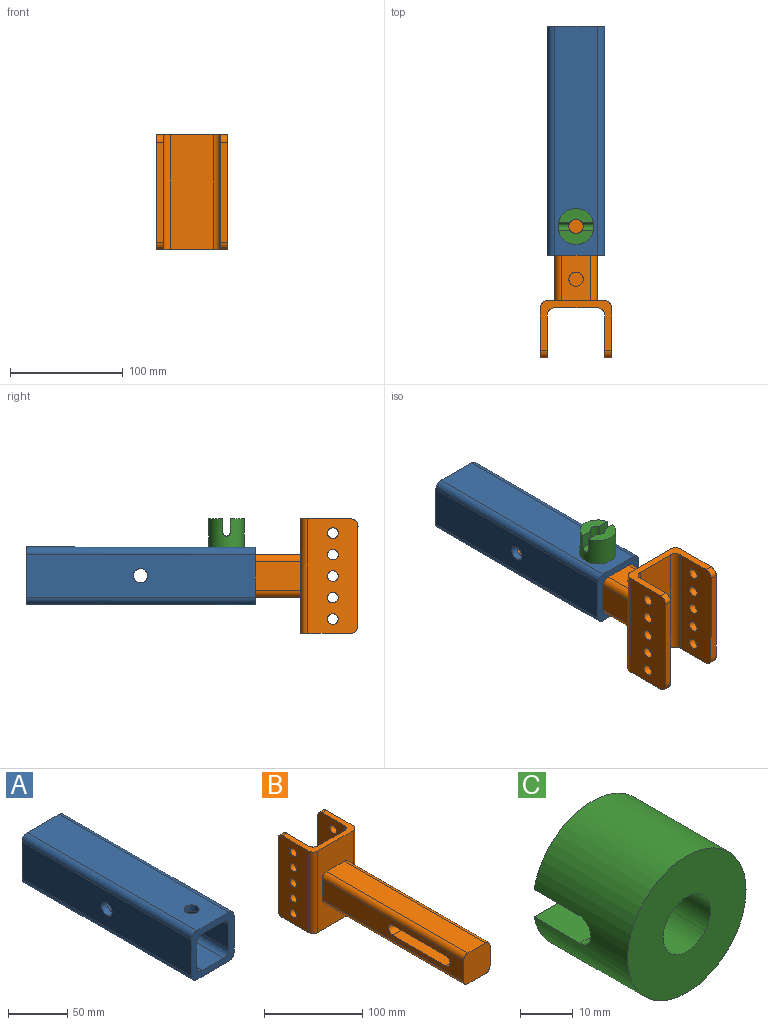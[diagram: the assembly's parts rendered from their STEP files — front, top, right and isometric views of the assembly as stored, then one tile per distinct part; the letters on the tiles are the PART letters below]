
ASSEMBLY  parts=3 mates=2
PART A: 21 faces, bbox 50.8x203.2x50.8 mm
  f0: plane 203.2x38.1mm, normal (-1,0,0), area 7615.2mm2, adj f1,f15,f16,f17,f19
  f1: cylinder r=6.35mm len=203.2mm, axis (0,1,0), area 2026.8mm2, adj f0,f2,f16,f17
  f2: plane 203.2x38.1mm, normal (0,0,-1), area 7741.9mm2, adj f1,f3,f16,f17
  f3: cylinder r=6.35mm len=203.2mm, axis (0,1,0), area 2026.8mm2, adj f2,f4,f16,f17
  f4: plane 203.2x38.1mm, normal (1,0,0), area 7615.2mm2, adj f3,f5,f16,f17,f18
  f5: cylinder r=6.35mm len=203.2mm, axis (0,1,0), area 2026.8mm2, adj f4,f6,f16,f17
  f6: plane 203.2x38.1mm, normal (0,0,1), area 7615.2mm2, adj f5,f15,f16,f17,f20
  f7: cylinder r=6.35mm len=203.2mm, axis (0,1,0), area 2026.8mm2, adj f8,f14,f16,f17
  f8: plane 203.2x25.4mm, normal (0,0,1), area 5161.3mm2, adj f7,f9,f16,f17
  f9: cylinder r=6.35mm len=203.2mm, axis (0,1,0), area 2026.8mm2, adj f8,f10,f16,f17
  f10: plane 203.2x25.4mm, normal (1,0,0), area 5034.6mm2, adj f9,f11,f16,f17,f19
  f11: cylinder r=6.35mm len=203.2mm, axis (0,1,0), area 2026.8mm2, adj f10,f12,f16,f17
  f12: plane 203.2x25.4mm, normal (0,0,-1), area 5034.6mm2, adj f11,f13,f16,f17,f20
  f13: cylinder r=6.35mm len=203.2mm, axis (0,1,0), area 2026.8mm2, adj f12,f14,f16,f17
  f14: plane 203.2x25.4mm, normal (-1,0,0), area 5034.6mm2, adj f7,f13,f16,f17,f18
  f15: cylinder r=6.35mm len=203.2mm, axis (0,1,0), area 2026.8mm2, adj f0,f6,f16,f17
  f16: plane 50.8x50.8mm, normal (0,-1,0), area 1129mm2, adj f0,f1,f2,f3,f4,f5,f6,f7
  f17: plane 50.8x50.8mm, normal (0,1,0), area 1129mm2, adj f0,f1,f2,f3,f4,f5,f6,f7
  f18: cylinder r=6.35mm len=12.7mm, axis (1,0,0), area 253.4mm2, adj f4,f14
  f19: cylinder r=6.35mm len=12.7mm, axis (1,0,0), area 253.4mm2, adj f0,f10
  f20: cylinder r=6.35mm len=12.7mm, axis (0,0,1), area 253.4mm2, adj f6,f12
PART B: 43 faces, bbox 63.5x254x101.6 mm
  f0: plane 203.2x25.4mm, normal (0,0,-1), area 5034.6mm2, adj f1,f7,f8,f13,f41
  f1: cylinder r=6.35mm len=203.2mm, axis (0,1,0), area 2026.8mm2, adj f0,f2,f8,f13
  f2: plane 203.2x25.4mm, normal (1,0,0), area 4066.9mm2, adj f1,f3,f8,f9,f10,f11,f12,f13
  f3: cylinder r=6.35mm len=203.2mm, axis (0,1,0), area 2026.8mm2, adj f2,f4,f8,f13
  f4: plane 203.2x25.4mm, normal (0,0,1), area 5161.3mm2, adj f3,f5,f8,f13
  f5: cylinder r=6.35mm len=203.2mm, axis (0,1,0), area 2026.8mm2, adj f4,f6,f8,f13
  f6: plane 203.2x25.4mm, normal (-1,0,0), area 4066.9mm2, adj f5,f7,f8,f9,f10,f11,f12,f13
  f7: cylinder r=6.35mm len=203.2mm, axis (0,1,0), area 2026.8mm2, adj f0,f6,f8,f13
  f8: plane 38.1x38.1mm, normal (0,-1,0), area 1417mm2, adj f0,f1,f2,f3,f4,f5,f6,f7
  f9: cylinder r=6.35mm len=38.1mm, axis (1,0,0), area 760.1mm2, adj f2,f6,f10,f12
  f10: plane 76.2x38.1mm, normal (0,0,-1), area 2903.2mm2, adj f2,f6,f9,f11
  f11: cylinder r=6.35mm len=38.1mm, axis (1,0,0), area 760.1mm2, adj f2,f6,f10,f12
  f12: plane 76.2x38.1mm, normal (0,0,1), area 2903.2mm2, adj f2,f6,f9,f11
  f13: plane 101.6x50.8mm, normal (0,-1,0), area 3744.3mm2, adj f0,f1,f2,f3,f4,f5,f6,f7
  f14: cylinder r=6.35mm len=101.6mm, axis (0,0,-1), area 1013.4mm2, adj f15,f24,f25,f26
  f15: plane 101.6x38.1mm, normal (0,1,0), area 3871mm2, adj f14,f16,f25,f26
  f16: cylinder r=6.35mm len=101.6mm, axis (0,0,-1), area 1013.4mm2, adj f15,f17,f25,f26
  f17: plane 101.6x38.1mm, normal (1,0,0), area 3497.4mm2, adj f16,f18,f25,f26,f32,f33,f34,f35
  f18: plane 88.9x6.35mm, normal (0,1,0), area 564.5mm2, adj f17,f19,f37,f40
  f19: plane 101.6x44.45mm, normal (-1,0,0), area 4142.5mm2, adj f18,f20,f25,f26,f32,f33,f34,f35
  f20: cylinder r=6.35mm len=101.6mm, axis (0,0,-1), area 1013.4mm2, adj f13,f19,f25,f26
  f21: cylinder r=6.35mm len=101.6mm, axis (0,0,-1), area 1013.4mm2, adj f13,f22,f25,f26
  f22: plane 101.6x44.45mm, normal (1,0,0), area 4142.5mm2, adj f21,f23,f25,f26,f27,f28,f29,f30
  f23: plane 88.9x6.35mm, normal (0,1,0), area 564.5mm2, adj f22,f24,f38,f39
  f24: plane 101.6x38.1mm, normal (-1,0,0), area 3497.4mm2, adj f14,f23,f25,f26,f27,f28,f29,f30
  f25: plane 63.5x44.45mm, normal (0,0,1), area 887.1mm2, adj f13,f14,f15,f16,f17,f19,f20,f21
  f26: plane 63.5x44.45mm, normal (0,0,-1), area 887.1mm2, adj f13,f14,f15,f16,f17,f19,f20,f21
  f27: cylinder r=4.76mm len=9.53mm, axis (1,0,0), area 190mm2, adj f22,f24
  f28: cylinder r=4.76mm len=9.53mm, axis (1,0,0), area 190mm2, adj f22,f24
  f29: cylinder r=4.76mm len=9.53mm, axis (1,0,0), area 190mm2, adj f22,f24
  f30: cylinder r=4.76mm len=9.53mm, axis (1,0,0), area 190mm2, adj f22,f24
  f31: cylinder r=4.76mm len=9.53mm, axis (1,0,0), area 190mm2, adj f22,f24
  f32: cylinder r=4.76mm len=9.53mm, axis (1,0,0), area 190mm2, adj f17,f19
  f33: cylinder r=4.76mm len=9.53mm, axis (1,0,0), area 190mm2, adj f17,f19
  f34: cylinder r=4.76mm len=9.53mm, axis (1,0,0), area 190mm2, adj f17,f19
  f35: cylinder r=4.76mm len=9.53mm, axis (1,0,0), area 190mm2, adj f17,f19
  f36: cylinder r=4.76mm len=9.53mm, axis (1,0,0), area 190mm2, adj f17,f19
  f37: cylinder r=6.35mm len=6.35mm, axis (-1,0,0), area 63.3mm2, adj f17,f18,f19,f26
  f38: cylinder r=6.35mm len=6.35mm, axis (-1,0,0), area 63.3mm2, adj f22,f23,f24,f26
  f39: cylinder r=6.35mm len=6.35mm, axis (1,0,0), area 63.3mm2, adj f22,f23,f24,f25
  f40: cylinder r=6.35mm len=6.35mm, axis (1,0,0), area 63.3mm2, adj f17,f18,f19,f25
  f41: cylinder r=6.35mm len=25.4mm, axis (0,0,-1), area 1013.4mm2, adj f0,f42
  f42: plane 12.7x12.7mm, normal (0,0,-1), area 126.7mm2, adj f41
PART C: 11 faces, bbox 31.8x25.4x31.8 mm
  f0: cylinder r=6.35mm len=25.4mm, axis (0,1,0), area 816.9mm2, adj f2,f3,f4,f5,f6,f7,f8,f9
  f1: cylinder r=15.88mm len=31.75mm, axis (0,1,0), area 2344.2mm2, adj f2,f3,f4,f5,f6,f7,f8,f9
  f2: plane 31.11x12.7mm, normal (0,1,0), area 271mm2, adj f0,f1,f7,f10
  f3: plane 31.75x31.75mm, normal (0,-1,0), area 665.1mm2, adj f0,f1
  f4: plane 31.11x12.7mm, normal (0,1,0), area 271mm2, adj f0,f1,f6,f9
  f5: cylinder r=3.17mm len=10.38mm, axis (-1,0,0), area 97.6mm2, adj f0,f1,f6,f7
  f6: plane 12.31x10.06mm, normal (0,0,-1), area 123.8mm2, adj f0,f1,f4,f5
  f7: plane 12.31x10.06mm, normal (0,0,1), area 123.8mm2, adj f0,f1,f2,f5
  f8: cylinder r=3.17mm len=10.38mm, axis (1,0,0), area 97.6mm2, adj f0,f1,f9,f10
  f9: plane 12.31x10.06mm, normal (0,0,-1), area 123.8mm2, adj f0,f1,f4,f8
  f10: plane 12.31x10.06mm, normal (0,0,1), area 123.8mm2, adj f0,f1,f2,f8
PLACE A rot(axis=(1,-0.05,0),0.1deg) t=(124.94,2.74,-77.56)mm
PLACE B rot(axis=(-1,0,0),179.9deg) t=(124.94,-240.88,-78)mm
PLACE C rot(axis=(0,0.71,0.71),180deg) t=(124.93,-175.15,-27.08)mm
MATE slider B.f8 <-> A.f16  axis (0,1,0) through (124.94,-37.68,-77.63)mm
MATE fastened C.f0 <-> A.f20  axis (0,0,-1) through (124.94,-175.11,-52.48)mm
